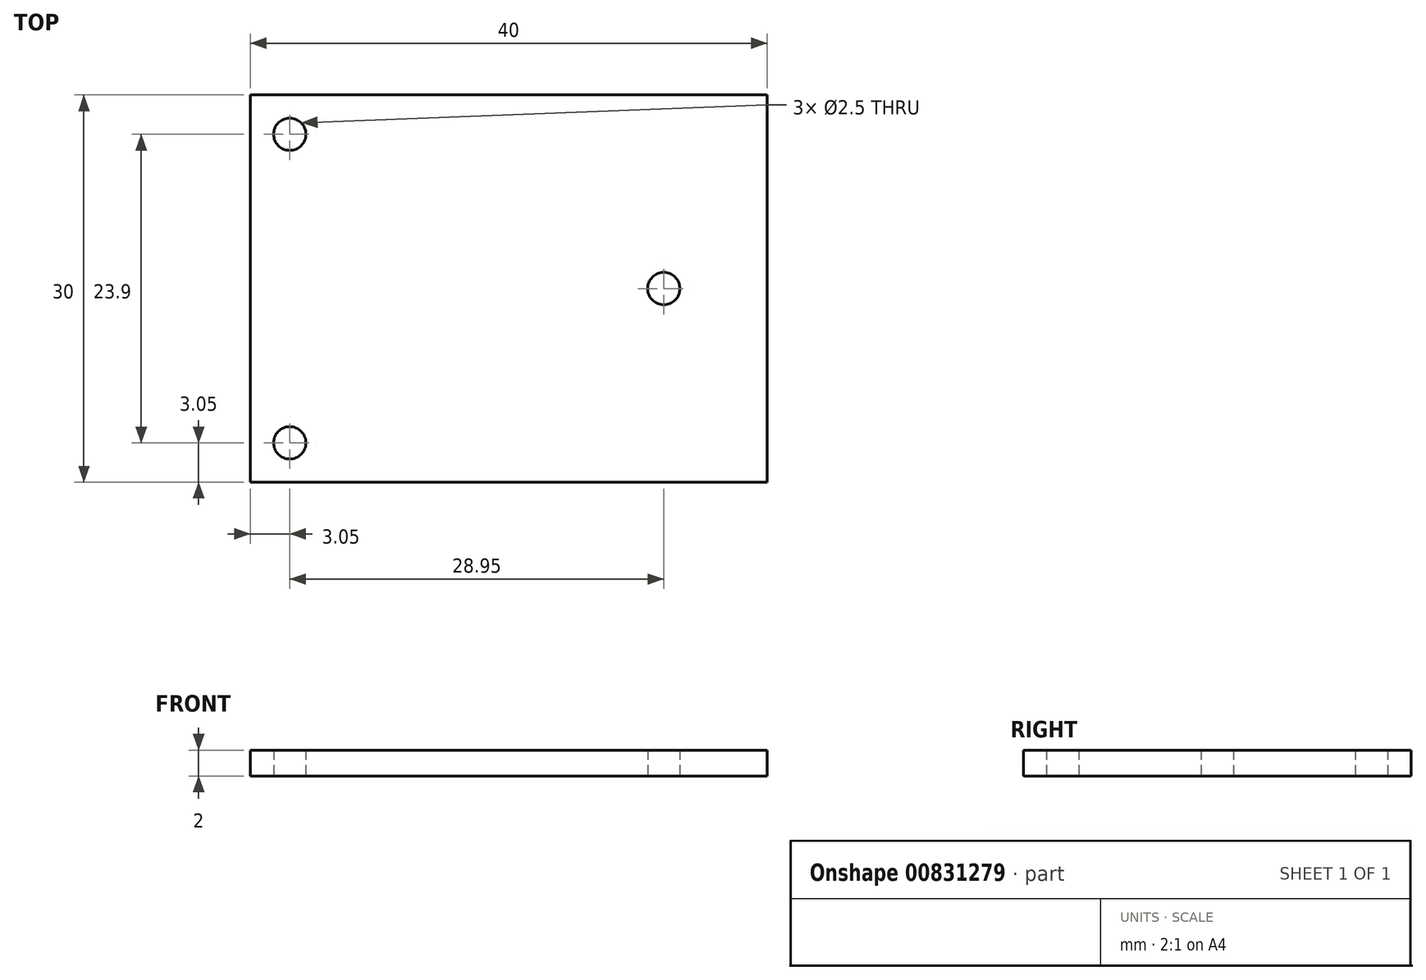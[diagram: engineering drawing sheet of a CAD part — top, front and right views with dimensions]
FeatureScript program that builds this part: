
annotation { "Feature Type Name" : "Feature", "Feature Type Description" : "" }
export const myFeature = defineFeature(function(context is Context, id is Id, definition is map)
    precondition{}
    {
        {
            var Q0;
            Q0=qCreatedBy(makeId("Top.planeOp"),FACE);
            var sketch = newSketch(context, id + "F0", { "sketchPlane" : qUnion([Q0])});
            skLineSegment(sketch, "E0.bottom", {"start": v(20, 15) * mm, "end": v(-20, 15) * mm});
            skLineSegment(sketch, "E0.top", {"start": v(20, -15) * mm, "end": v(-20, -15) * mm});
            skLineSegment(sketch, "E0.left", {"start": v(20, 15) * mm, "end": v(20, -15) * mm});
            skLineSegment(sketch, "E0.right", {"start": v(-20, 15) * mm, "end": v(-20, -15) * mm});
            skPoint(sketch, "E0.middle", {"position": v(0, 0) * mm});
            skCircle(sketch, "E1", {"center": v(-16.95, 11.95) * mm, "radius": 1.25 * mm});
            skCircle(sketch, "E2", {"center": v(-16.95, -11.95) * mm, "radius": 1.25 * mm});
            skCircle(sketch, "E3", {"center": v(12, 0) * mm, "radius": 1.25 * mm});
            skSolve(sketch);
        }
        {
            var Q0;
            Q0=qSketchRegion(id+"F0",true);
            extrude(context, id + "F1", {"entities" : qUnion([Q0]), "depth" : 2 * mm, "offsetDistance" : 25.4 * mm});
        }
    });
